# Revit family: НЕВАТОМ_Кожух защиты электродвигателя ВР 280-46 (Исп. 1), Версия 1
name_source: partatom
category: Оборудование
revit_build: Autodesk Revit 2017 (Build: 20170118_1100(x64)
units: mm (PartAtom-declared; Revit-internal decimal feet)

## family parameters
Всегда вертикально = Да
На основе рабочей плоскости = Нет
Общий = Нет
При загрузке вырезать с полостями = Нет
Размер круглого соединителя = Использовать диаметр
Тип детали = Нормальный
Точка расчета площади = Нет

## types (1)
- Кожух защиты электродвигателя ВР-280-46 (Исполнение 1)
    A = 98 мм
    ADSK_Единица измерения = шт.
    ADSK_Завод-изготовитель = НЕВАТОМ
    ADSK_Масса = 0
    ADSK_Наименование = Кожух защиты электродвигателя ВР-280-46-2.0 (Исп. 1)
    B = 208 мм
    H = 100 мм
    Hm = -95 мм
    L = 330 мм
    Lm = 31 мм
    Ln = 328 мм
    T1 = 206 мм
    T2 = 96 мм
    VR = 2
    t = 1 мм
    Исполнение = Исполнение 1
    Кожух = НЕВАТОМ_Кожух защиты электродвигателя ВР 280-46, Исполнение 1
    Материал = Сталь оцинкованная
